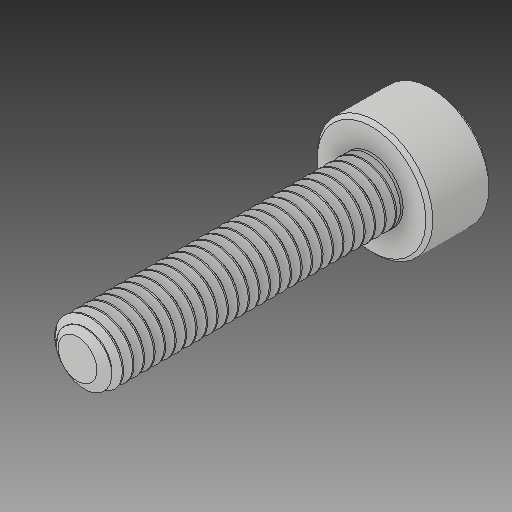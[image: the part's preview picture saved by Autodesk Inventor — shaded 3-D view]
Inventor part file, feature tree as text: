
AUTODESK INVENTOR PART (.ipt)
format: ipt  version: 2019.4 (Build 234330000, 330)  size: 960,000 bytes
history: native  units: in
note: dims shown in document units (in); Inventor stores cm internally (conversion verified against a paired STEP export)
features: revolve x1
ambient origin geometry x8: Origin, YZ Plane, XZ Plane, XY Plane, X Axis, Y Axis, Z Axis, Center Point
bodies: Solid1 (feature_tree)
feature tree (1):
  revolve  "Revolve1"  [1 undecoded]
note: 1 required parameter value undecoded (feature->parameter linkage not recoverable at this tier; creation-order binding heuristic only, values carry confidence <= 0.55)
